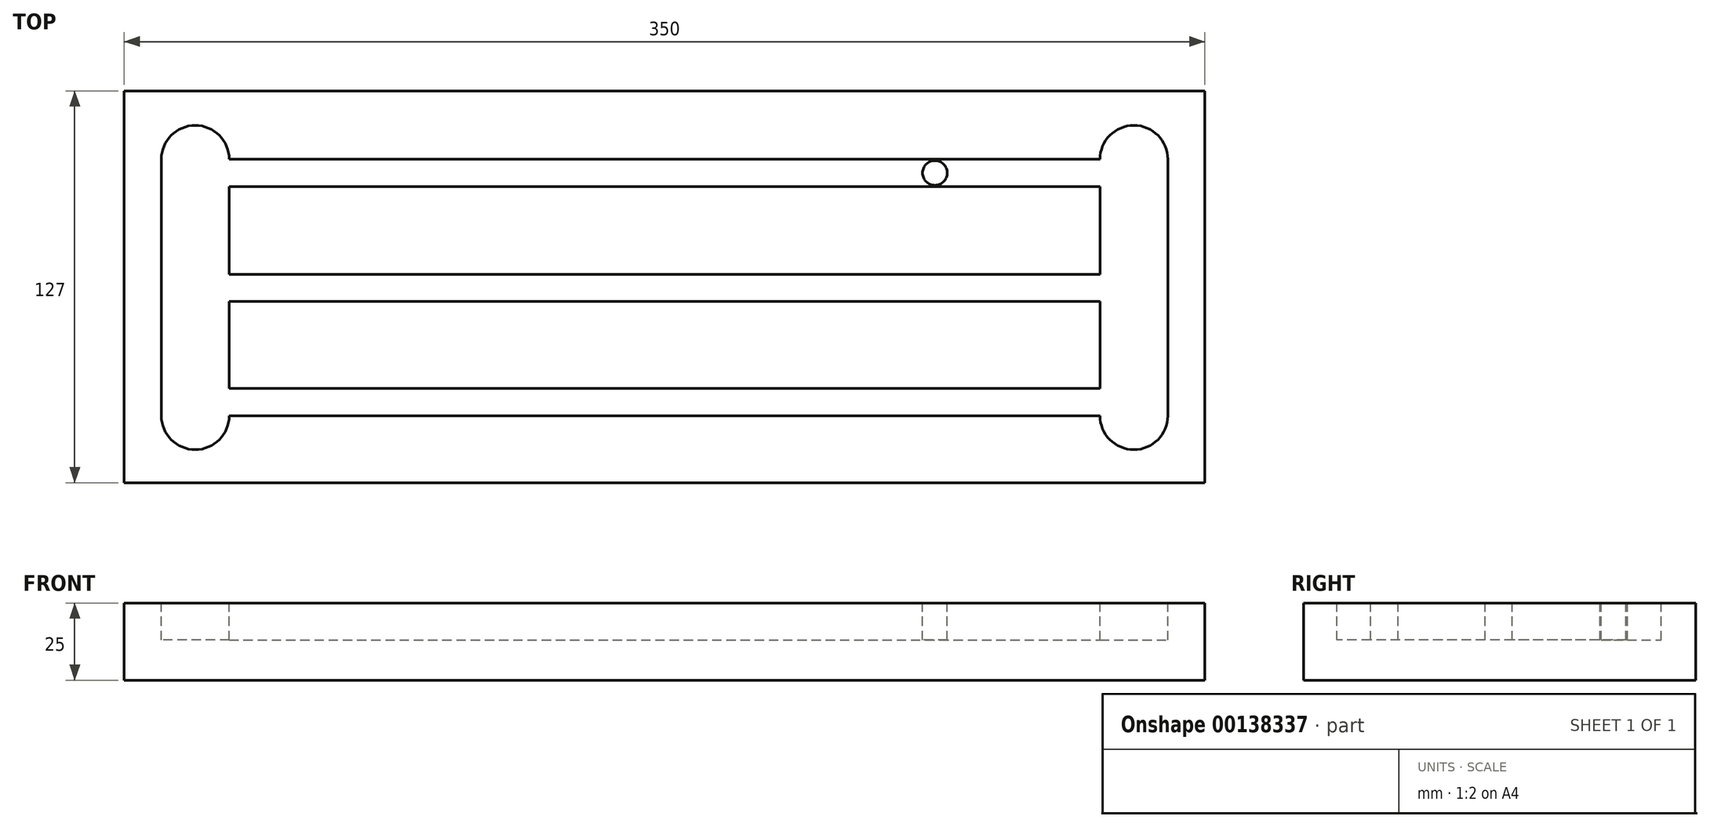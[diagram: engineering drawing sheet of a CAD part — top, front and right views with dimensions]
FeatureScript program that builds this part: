
annotation { "Feature Type Name" : "Feature", "Feature Type Description" : "" }
export const myFeature = defineFeature(function(context is Context, id is Id, definition is map)
    precondition{}
    {
        {
            var Q0;
            Q0=qCreatedBy(makeId("Top.planeOp"),FACE);
            var sketch = newSketch(context, id + "F0", { "sketchPlane" : qUnion([Q0])});
            skLineSegment(sketch, "E0.bottom", {"start": v(0, 0) * mm, "end": v(350, 0) * mm});
            skLineSegment(sketch, "E0.top", {"start": v(0, -127) * mm, "end": v(350, -127) * mm});
            skLineSegment(sketch, "E0.left", {"start": v(0, 0) * mm, "end": v(0, -127) * mm});
            skLineSegment(sketch, "E0.right", {"start": v(350, 0) * mm, "end": v(350, -127) * mm});
            skSolve(sketch);
        }
        {
            var Q0;
            Q0=makeQuery(id+"F0.imprint","IMPRINT",FACE,{"disambiguationData":[TD([[makeQuery(id+"F0.imprint","IMPRINT",EDGE,{"derivedFrom":sQuery(id+"F0.wireOp",EDGE,"E0.bottom")}),-1.0]])]});
            extrude(context, id + "F1", {"entities" : qUnion([Q0]), "flatOperationType" : FlatOperationType.REMOVE, "offsetDistance" : 25 * mm, "depth" : 25 * mm, "domain" : OperationDomain.MODEL});
        }
        {
            var Q0;
            Q0=makeQuery(id+"F1.opExtrude","CAP_FACE",FACE,{"disambiguationData":[OSD([sQuery(id+"F0.wireOp",EDGE,"E0.bottom"),sQuery(id+"F0.wireOp",EDGE,"E0.top"),sQuery(id+"F0.wireOp",EDGE,"E0.left"),sQuery(id+"F0.wireOp",EDGE,"E0.right")])],"isStart":false});
            var sketch = newSketch(context, id + "F2", { "sketchPlane" : qUnion([Q0])});
            skLineSegment(sketch, "E1.bottom", {"start": v(34, -22.2) * mm, "end": v(316, -22.2) * mm});
            skLineSegment(sketch, "E1.top", {"start": v(34, -105.3) * mm, "end": v(316, -105.3) * mm});
            skLineSegment(sketch, "E1.left", {"start": v(12, -22.2) * mm, "end": v(12, -105.3) * mm});
            skLineSegment(sketch, "E1.right", {"start": v(338, -22.2) * mm, "end": v(338, -105.3) * mm});
            skLineSegment(sketch, "E2.bottom", {"start": v(34, -31) * mm, "end": v(316, -31) * mm});
            skLineSegment(sketch, "E2.top", {"start": v(34, -59.5) * mm, "end": v(316, -59.5) * mm});
            skLineSegment(sketch, "E3.bottom", {"start": v(34, -68.3) * mm, "end": v(316, -68.3) * mm});
            skLineSegment(sketch, "E3.top", {"start": v(34, -96.5) * mm, "end": v(316, -96.5) * mm});
            skLineSegment(sketch, "E4", {"start": v(34, -31) * mm, "end": v(34, -59.5) * mm});
            skLineSegment(sketch, "E5", {"start": v(316, -31) * mm, "end": v(316, -59.5) * mm});
            skLineSegment(sketch, "E6.trimOffspring", {"start": v(34, -68.3) * mm, "end": v(34, -96.5) * mm});
            skLineSegment(sketch, "E7.trimOffspring", {"start": v(316, -68.3) * mm, "end": v(316, -96.5) * mm});
            skArc(sketch, "E8", {"start": v(34, -22.2) * mm, "mid": v(23, -11.2) * mm, "end": v(12, -22.2) * mm});
            skArc(sketch, "E9", {"start": v(12, -105.3) * mm, "mid": v(23, -116.3) * mm, "end": v(34, -105.3) * mm});
            skArc(sketch, "E10", {"start": v(338, -22.2) * mm, "mid": v(327, -11.2) * mm, "end": v(316, -22.2) * mm});
            skArc(sketch, "E11", {"start": v(316, -105.3) * mm, "mid": v(327, -116.3) * mm, "end": v(338, -105.3) * mm});
            skCircle(sketch, "E12", {"center": v(262.54, -26.6) * mm, "radius": 4 * mm});
            skSolve(sketch);
        }
        {
            var Q0;
            Q0=makeQuery(id+"F2.imprint","IMPRINT",FACE,{"disambiguationData":[TD([[makeQuery(id+"F2.imprint","IMPRINT",EDGE,{"derivedFrom":sQuery(id+"F2.wireOp",EDGE,"E1.bottom")}),-1.0]])]});
            extrude(context, id + "F3", {"entities" : qUnion([Q0]), "operationType" : NewBodyOperationType.REMOVE, "oppositeDirection" : true, "depth" : 12 * mm});
        }
    });
